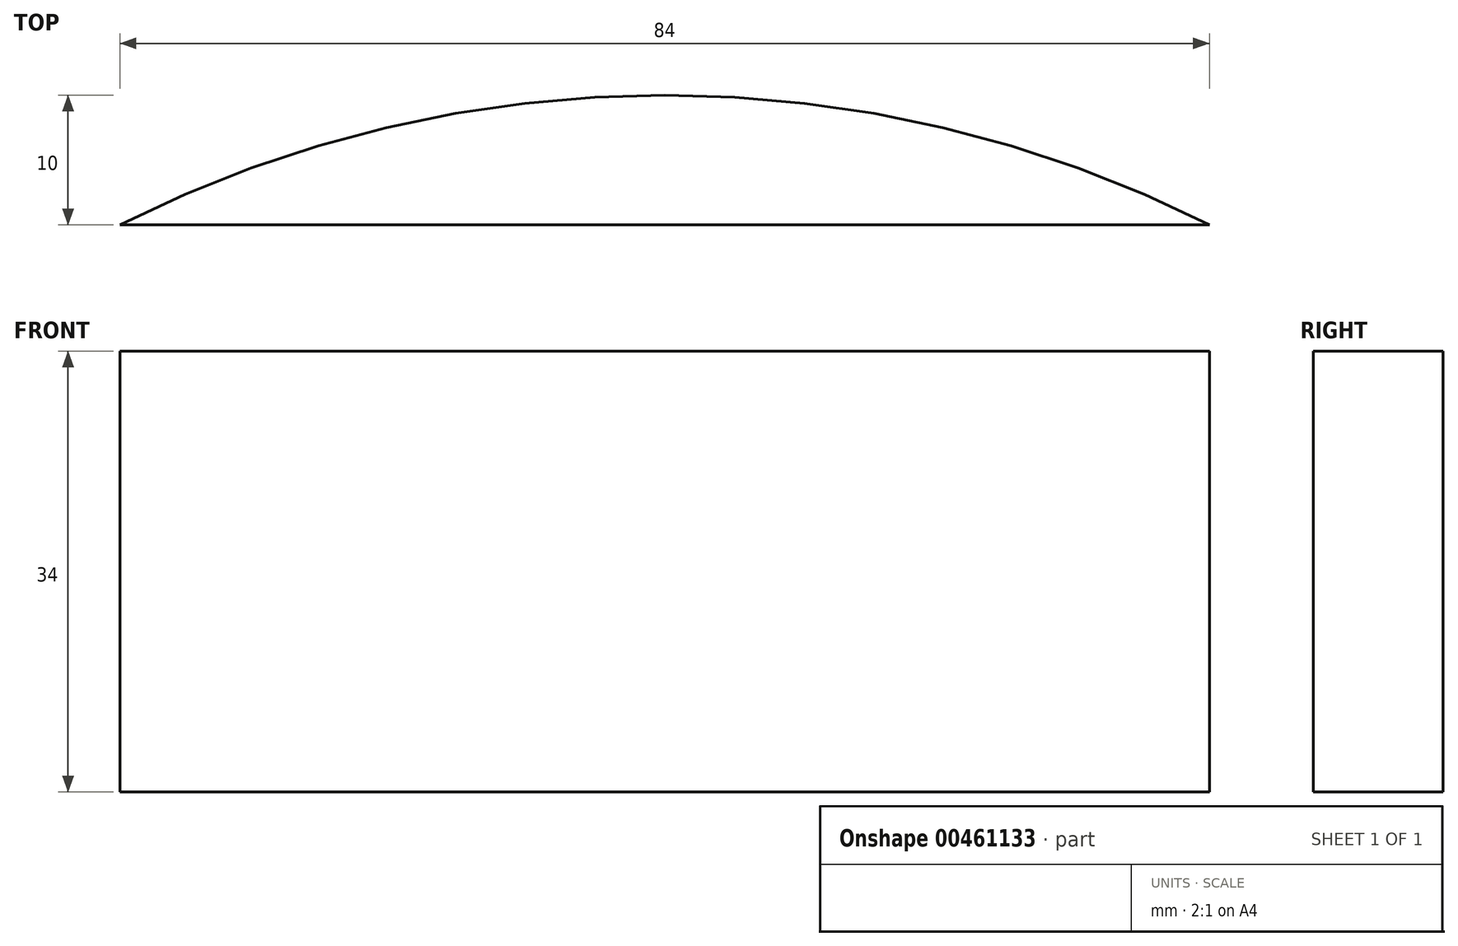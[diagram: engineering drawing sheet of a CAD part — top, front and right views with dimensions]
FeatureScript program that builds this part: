
annotation { "Feature Type Name" : "Feature", "Feature Type Description" : "" }
export const myFeature = defineFeature(function(context is Context, id is Id, definition is map)
    precondition{}
    {
        {
            var Q0;
            Q0=qCreatedBy(makeId("Top.planeOp"),FACE);
            var sketch = newSketch(context, id + "F0", { "sketchPlane" : qUnion([Q0])});
            skLineSegment(sketch, "E0", {"start": v(-52.77, -4.06) * mm, "end": v(31.23, -4.06) * mm});
            skLineSegment(sketch, "E1", {"start": v(-10.77, -4.06) * mm, "end": v(-10.77, 5.94) * mm, "construction": true});
            skArc(sketch, "E2", {"start": v(31.23, -4.06) * mm, "mid": v(-10.77, 5.94) * mm, "end": v(-52.77, -4.06) * mm});
            skSolve(sketch);
        }
        {
            var Q0;
            Q0 = qSketchRegion(id + "F0", true);
            extrude(context, id + "F1", {"entities" : qUnion([Q0]), "depth" : 34 * mm});
        }
    });
